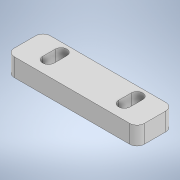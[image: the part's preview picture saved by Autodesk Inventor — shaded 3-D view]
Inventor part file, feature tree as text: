
AUTODESK INVENTOR PART (.ipt)
format: ipt  version: 2021 (Build 250183000, 183)  size: 121,344 bytes
history: native  units: mm
features: extrude x1, fillet x1, sketch x1
ambient origin geometry x8: Origin, YZ Plane, XZ Plane, XY Plane, X Axis, Y Axis, Z Axis, Center Point
bodies: Solid1 (feature_tree)
feature tree (3):
  extrude  "Extrusion1"  Depth=10.0mm
  fillet  "Fillet1"  Radius=21.0mm
  sketch  "Sketch1"  dims[d0=36.0mm d1=10.0mm d2=21.0mm d3=3.5mm d4=3.2mm d5=2.5mm d6=5.0mm d7=0.0mm d8=2.0mm]
